# Revit family: TSL_US - TSL980 - Straight Spout Tap Small
name_source: partatom
category: Plumbing Fixtures
units: mm (PartAtom-declared; Revit-internal decimal feet)

## family parameters
Always vertical = Yes
Cut with Voids When Loaded = No
Part Type = Normal
Room Calculation Point = No
Round Connector Dimension = Use Diameter
Shared = No
Work Plane-Based = Yes

## types (5) — shared parameters
Assembly Code = D2010900
Default Elevation = 0' - 0"
Description = The TSL.980 is a stainless steel deck mounted sensor tap, available in a variety of coloured finished, with a sleek and minimalist design.
Keynote = 22 40 00
Manufacturer = The Splash Lab
TSL Connector Diameter = 0' - 0 1/2"
Type Comments = STRAIGHT SPOUT FAUCET SMALL
Type Image = <None>
URL = https://thesplashlab.com

## per-type parameters (varying)
| type | Model | TSL Material 01 |
| TSL.980.CS - Satin | TSL.980.CS | TSL - Material - Satin |
| TSL.980.CP - Copper | TSL.980.CP | TSL - Material - Copper |
| TSL.980.BR - Brass | TSL.980.BR | TSL - Material - Brass |
| TSL.980.BK - Black | TSL.980.BK | TSL - Material - Black |
| TSL.980.BZ - Bronze | TSL.980.BZ | TSL - Material - Bronze |

## geometry (parser evidence)
native form markers: Sweep x2
no freeform markers — native parametric forms only
